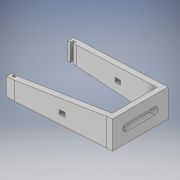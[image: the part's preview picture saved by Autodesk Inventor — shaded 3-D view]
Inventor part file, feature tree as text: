
AUTODESK INVENTOR PART (.ipt)
format: ipt  version: 2019 (Build 230136000, 136)  size: 165,376 bytes
history: native  units: mm
features: extrude x3, sketch x3, mirror x1, draft x1
ambient origin geometry x8: Origin, YZ Plane, XZ Plane, XY Plane, X Axis, Y Axis, Z Axis, Center Point
bodies: Solid1 (feature_tree)
feature tree (8):
  extrude  "Extrusion1"  Depth=22.0mm
  mirror  "Mirror1"
  draft  "FaceDraft1"
  extrude  "Extrusion2"  Depth=2.0mm
  extrude  "Extrusion3"  Depth=10.0mm
  sketch  "Sketch1"  dims[d0=1.0mm d1=22.0mm]
  sketch  "Sketch2"  dims[d2=3.0mm d3=2.0mm]
  sketch  "Sketch3"  dims[d4=2.0mm d5=10.0mm d6=35.0mm d7=10.0mm d8=0.0mm d9=1.047198mm d10=2.0mm d11=1.5mm d12=3.0mm d13=18.0mm d14=10.0mm d15=0.0mm d16=5.0mm d17=2.5mm d18=10.0mm d19=0.0mm]
